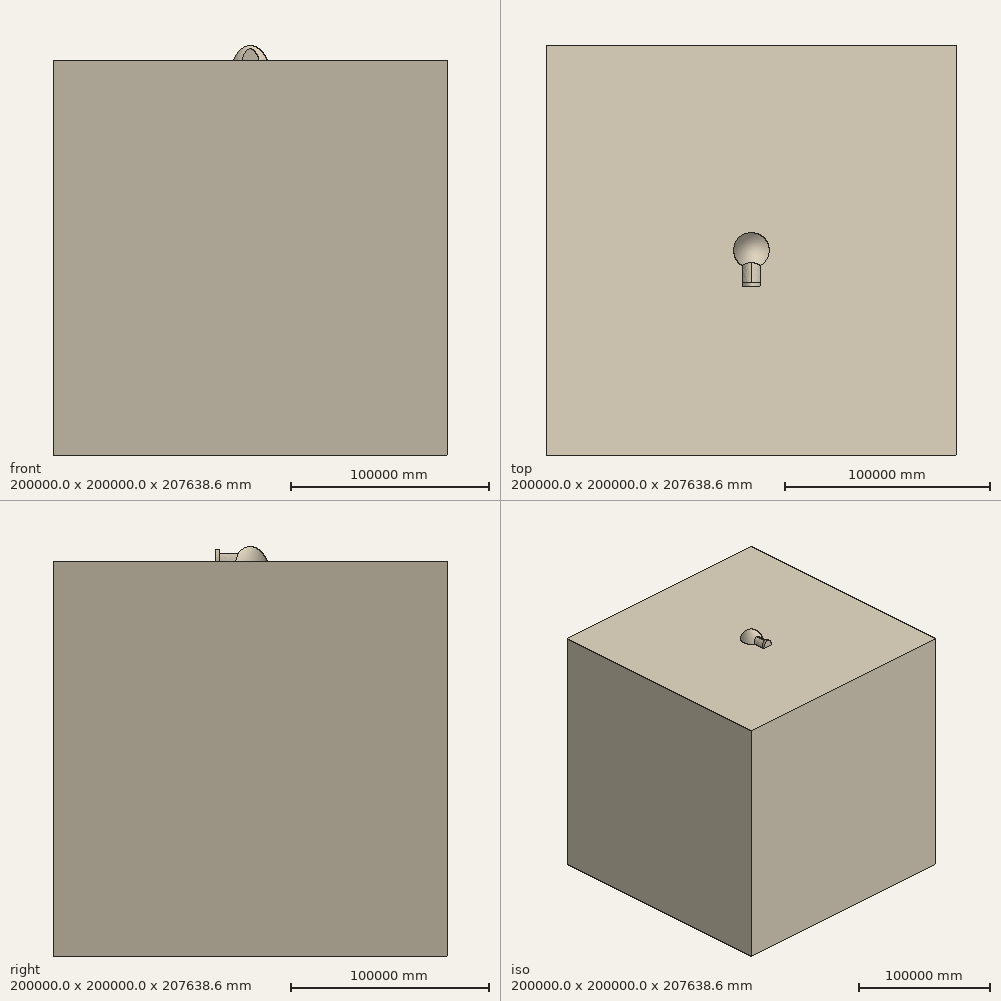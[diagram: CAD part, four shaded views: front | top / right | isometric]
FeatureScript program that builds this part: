
annotation { "Feature Type Name" : "Feature", "Feature Type Description" : "" }
export const myFeature = defineFeature(function(context is Context, id is Id, definition is map)
    precondition{}
    {
        {
            var Q0;
            Q0=qCreatedBy(makeId("Right.planeOp"),FACE);
            var sketch = newSketch(context, id + "F0", { "sketchPlane" : qUnion([Q0])});
            skFitSpline(sketch, "E0", {"points": [v(0, 7638.6) * mm, v(29.11, 7638.5) * mm, v(87.34, 7638.32) * mm, v(174.7, 7636.6) * mm, v(262.04, 7633.45) * mm, v(349.4, 7629.03) * mm, v(436.75, 7623.3) * mm, v(524.1, 7616.28) * mm, v(611.46, 7607.96) * mm, v(698.83, 7598.34) * mm, v(786.2, 7587.4) * mm, v(873.57, 7575.22) * mm, v(960.93, 7561.56) * mm, v(1048.3, 7546.64) * mm, v(1135.69, 7530.43) * mm, v(1223.06, 7512.8) * mm, v(1310.44, 7493.87) * mm, v(1397.81, 7473.6) * mm, v(1485.24, 7452.19) * mm, v(1572.58, 7429.04) * mm, v(1660, 7404.87) * mm, v(1747.4, 7379.26) * mm, v(1834.8, 7352.23) * mm, v(1922.16, 7323.74) * mm, v(2009.63, 7294.12) * mm, v(2096.98, 7262.8) * mm, v(2184.4, 7230.3) * mm, v(2271.83, 7196.4) * mm, v(2359.23, 7161.05) * mm, v(2446.66, 7124.32) * mm, v(2534.07, 7086.12) * mm, v(2621.48, 7046.47) * mm, v(2708.92, 7005.43) * mm, v(2796.34, 6962.93) * mm, v(2883.78, 6919) * mm, v(2971.2, 6873.54) * mm, v(3058.64, 6826.64) * mm, v(3146.12, 6778.32) * mm, v(3233.5, 6728.33) * mm, v(3321, 6676.98) * mm, v(3408.41, 6624) * mm, v(3495.88, 6569.56) * mm, v(3583.33, 6513.57) * mm, v(3670.8, 6456.03) * mm, v(3758.23, 6396.86) * mm, v(3845.74, 6336.2) * mm, v(3933.18, 6273.83) * mm, v(4020.62, 6209.87) * mm, v(4108.17, 6144.41) * mm, v(4195.58, 6077.13) * mm, v(4283.07, 6008.28) * mm, v(4370.6, 5937.8) * mm, v(4458.06, 5865.55) * mm, v(4545.5, 5791.58) * mm, v(4633.1, 5716.02) * mm, v(4720.52, 5638.55) * mm, v(4808.02, 5559.39) * mm, v(4895.58, 5478.53) * mm, v(4983, 5395.75) * mm, v(5070.6, 5311.3) * mm, v(5158.05, 5224.92) * mm, v(5245.61, 5136.77) * mm, v(5333.08, 5046.68) * mm, v(5420.71, 4954.83) * mm, v(5508.13, 4860.86) * mm, v(5595.7, 4765.1) * mm, v(5683.29, 4667.42) * mm, v(5770.79, 4567.66) * mm, v(5858.29, 4465.9) * mm, v(5945.9, 4362.23) * mm, v(6033.45, 4256.45) * mm, v(6120.96, 4148.6) * mm, v(6208.56, 4038.73) * mm, v(6296.18, 3926.74) * mm, v(6383.62, 3812.49) * mm, v(6471.32, 3696.22) * mm, v(6558.84, 3577.65) * mm, v(6646.38, 3456.9) * mm, v(6734.07, 3334) * mm, v(6821.65, 3208.74) * mm, v(6909.12, 3081.1) * mm, v(6996.88, 2951.3) * mm, v(7084.42, 2819.04) * mm, v(7171.98, 2684.38) * mm, v(7259.68, 2547.4) * mm, v(7347.3, 2407.92) * mm, v(7434.81, 2265.88) * mm, v(7522.6, 2121.48) * mm, v(7610.17, 1974.42) * mm, v(7697.73, 1824.78) * mm, v(7785.52, 1672.67) * mm, v(7873.1, 1517.81) * mm, v(7960.7, 1360.25) * mm, v(8048.5, 1200.06) * mm, v(8136.08, 1037.02) * mm, v(8223.73, 871.22) * mm, v(8311.5, 702.68) * mm, v(8399.14, 531.2) * mm, v(8486.77, 356.8) * mm, v(8574.63, 179.6) * mm, v(8632.51, 60.13) * mm, v(8661.64, 0) * mm]});
            skFitSpline(sketch, "E1", {"points": [v(0, 5583.5) * mm, v(20.7, 5583.4) * mm, v(62.09, 5583.2) * mm, v(124.17, 5581.72) * mm, v(186.27, 5579.52) * mm, v(248.34, 5576) * mm, v(310.44, 5571.88) * mm, v(372.53, 5566.67) * mm, v(434.62, 5560.43) * mm, v(496.71, 5553.37) * mm, v(558.8, 5545.24) * mm, v(620.87, 5536.23) * mm, v(682.98, 5526.4) * mm, v(745.05, 5515.32) * mm, v(807.13, 5503.42) * mm, v(869.25, 5490.68) * mm, v(931.3, 5476.72) * mm, v(993.4, 5461.91) * mm, v(1055.54, 5446.27) * mm, v(1117.58, 5429.42) * mm, v(1179.67, 5411.72) * mm, v(1241.74, 5393.02) * mm, v(1303.85, 5373.32) * mm, v(1365.95, 5352.61) * mm, v(1428.03, 5330.92) * mm, v(1490.11, 5308.21) * mm, v(1552.15, 5284.38) * mm, v(1614.27, 5259.7) * mm, v(1676.4, 5234) * mm, v(1738.46, 5207.2) * mm, v(1800.53, 5179.37) * mm, v(1862.6, 5150.48) * mm, v(1924.69, 5120.56) * mm, v(1986.86, 5089.7) * mm, v(2048.86, 5057.51) * mm, v(2111.05, 5024.62) * mm, v(2173.01, 4990.3) * mm, v(2235.17, 4955.18) * mm, v(2297.21, 4918.72) * mm, v(2359.34, 4881.33) * mm, v(2421.46, 4842.87) * mm, v(2483.46, 4803.09) * mm, v(2545.55, 4762.32) * mm, v(2607.69, 4720.42) * mm, v(2669.75, 4677.29) * mm, v(2731.88, 4633.13) * mm, v(2793.9, 4587.66) * mm, v(2855.96, 4541.07) * mm, v(2918.13, 4493.39) * mm, v(2980.15, 4444.35) * mm, v(3042.32, 4394.3) * mm, v(3104.3, 4342.8) * mm, v(3166.43, 4290.26) * mm, v(3228.49, 4236.33) * mm, v(3290.62, 4181.23) * mm, v(3352.72, 4124.85) * mm, v(3414.72, 4067.08) * mm, v(3476.83, 4008.11) * mm, v(3538.92, 3947.8) * mm, v(3601.06, 3886.2) * mm, v(3663.11, 3823.17) * mm, v(3725.26, 3758.91) * mm, v(3787.2, 3693.12) * mm, v(3849.39, 3626.16) * mm, v(3911.44, 3557.64) * mm, v(3973.54, 3487.73) * mm, v(4035.68, 3416.46) * mm, v(4097.63, 3343.58) * mm, v(4159.78, 3269.41) * mm, v(4221.87, 3193.7) * mm, v(4283.96, 3116.48) * mm, v(4346.1, 3037.8) * mm, v(4408.04, 2957.44) * mm, v(4470.2, 2875.66) * mm, v(4532.28, 2792.25) * mm, v(4594.37, 2707.23) * mm, v(4656.52, 2620.65) * mm, v(4718.46, 2532.3) * mm, v(4780.57, 2442.42) * mm, v(4842.72, 2350.88) * mm, v(4904.79, 2257.6) * mm, v(4966.88, 2162.58) * mm, v(5029.02, 2065.9) * mm, v(5091, 1967.32) * mm, v(5153.08, 1867.07) * mm, v(5215.23, 1765.02) * mm, v(5277.3, 1661.1) * mm, v(5339.44, 1555.34) * mm, v(5401.36, 1447.59) * mm, v(5463.54, 1338.08) * mm, v(5525.6, 1226.58) * mm, v(5587.74, 1113.15) * mm, v(5649.82, 997.72) * mm, v(5711.8, 880.2) * mm, v(5773.93, 760.75) * mm, v(5836.02, 639.2) * mm, v(5898.12, 515.55) * mm, v(5960.25, 389.81) * mm, v(6022.2, 261.83) * mm, v(6084.37, 131.79) * mm, v(6125.36, 44.13) * mm, v(6146, 0) * mm]});
            skLineSegment(sketch, "E2", {"start": v(6146, 0) * mm, "end": v(8661.64, 0) * mm});
            skLineSegment(sketch, "E3", {"start": v(0, 5583.5) * mm, "end": v(0, 7638.6) * mm});
            skLineSegment(sketch, "E4", {"start": v(0, 0) * mm, "end": v(13207.23, 0) * mm});
            skLineSegment(sketch, "E5", {"start": v(0, 0) * mm, "end": v(0, 9039.67) * mm, "construction": true});
            skSolve(sketch);
        }
        {
            var Q0;
            Q0=qSketchRegion(id+"F0",true);
            var Q1;
            Q1=sQuery(id+"F0.wireOp",EDGE,"E3");
            revolve(context, id + "F1", {"surfaceOperationType" : NewSurfaceOperationType.NEW, "entities" : qUnion([Q0]), "axis" : qUnion([Q1]), "revolveType" : RevolveType.FULL});
        }
        {
            var Q0;
            Q0=qCreatedBy(makeId("Front.planeOp"),FACE);
            var sketch = newSketch(context, id + "F2", { "sketchPlane" : qUnion([Q0])});
            skFitSpline(sketch, "E6", {"points": [v(-2323.2, 0) * mm, v(-2315.44, 23.67) * mm, v(-2300.04, 70.61) * mm, v(-2276.5, 140.2) * mm, v(-2252.98, 208.44) * mm, v(-2229.63, 275.42) * mm, v(-2206.1, 341.03) * mm, v(-2182.58, 405.35) * mm, v(-2159.23, 468.49) * mm, v(-2135.7, 530.32) * mm, v(-2112.18, 590.94) * mm, v(-2088.82, 650.42) * mm, v(-2065.3, 708.67) * mm, v(-2041.78, 765.76) * mm, v(-2018.42, 821.79) * mm, v(-1994.9, 876.63) * mm, v(-1971.37, 930.37) * mm, v(-1948.01, 983.11) * mm, v(-1924.53, 1034.72) * mm, v(-1900.94, 1085.25) * mm, v(-1877.65, 1134.87) * mm, v(-1854.07, 1183.38) * mm, v(-1830.58, 1230.94) * mm, v(-1807.22, 1277.6) * mm, v(-1783.68, 1323.2) * mm, v(-1760.2, 1367.85) * mm, v(-1736.8, 1411.63) * mm, v(-1713.26, 1454.42) * mm, v(-1689.8, 1496.37) * mm, v(-1666.38, 1537.46) * mm, v(-1642.9, 1577.62) * mm, v(-1619.36, 1616.9) * mm, v(-1595.99, 1655.47) * mm, v(-1572.51, 1693.13) * mm, v(-1548.93, 1729.93) * mm, v(-1525.63, 1766.08) * mm, v(-1502.05, 1801.27) * mm, v(-1478.58, 1835.73) * mm, v(-1455.2, 1869.5) * mm, v(-1431.66, 1902.38) * mm, v(-1408.17, 1934.6) * mm, v(-1384.7, 1966.05) * mm, v(-1361.24, 1996.83) * mm, v(-1337.8, 2026.9) * mm, v(-1314.26, 2056.17) * mm, v(-1290.85, 2084.85) * mm, v(-1267.38, 2112.82) * mm, v(-1243.87, 2140.09) * mm, v(-1220.45, 2166.76) * mm, v(-1196.98, 2192.73) * mm, v(-1173.44, 2218) * mm, v(-1150.09, 2242.78) * mm, v(-1126.51, 2266.74) * mm, v(-1103.09, 2290.22) * mm, v(-1079.65, 2313.09) * mm, v(-1056.12, 2335.26) * mm, v(-1032.7, 2356.94) * mm, v(-1009.21, 2378) * mm, v(-985.76, 2398.47) * mm, v(-962.3, 2418.38) * mm, v(-938.8, 2437.68) * mm, v(-915.36, 2456.49) * mm, v(-891.9, 2474.7) * mm, v(-868.36, 2492.27) * mm, v(-845, 2509.53) * mm, v(-821.42, 2525.97) * mm, v(-798.03, 2542.13) * mm, v(-774.52, 2557.6) * mm, v(-751.06, 2572.61) * mm, v(-727.59, 2587.12) * mm, v(-704.12, 2601.12) * mm, v(-680.65, 2614.62) * mm, v(-657.18, 2627.62) * mm, v(-633.71, 2640.13) * mm, v(-610.24, 2652.13) * mm, v(-586.77, 2663.64) * mm, v(-563.28, 2674.62) * mm, v(-539.86, 2685.27) * mm, v(-516.34, 2695.22) * mm, v(-492.88, 2704.84) * mm, v(-469.42, 2714.06) * mm, v(-445.95, 2722.75) * mm, v(-422.48, 2730.96) * mm, v(-399, 2738.64) * mm, v(-375.54, 2745.97) * mm, v(-352.05, 2752.75) * mm, v(-328.58, 2759.14) * mm, v(-305.15, 2765.21) * mm, v(-281.63, 2770.51) * mm, v(-258.19, 2775.69) * mm, v(-234.72, 2780.29) * mm, v(-211.22, 2784.31) * mm, v(-187.79, 2788.24) * mm, v(-164.28, 2791.31) * mm, v(-140.83, 2794.3) * mm, v(-117.35, 2796.68) * mm, v(-93.88, 2798.56) * mm, v(-70.41, 2800.07) * mm, v(-46.94, 2801.16) * mm, v(-23.47, 2801.9) * mm, v(0, 2802.05) * mm, v(23.47, 2801.9) * mm, v(46.94, 2801.16) * mm, v(70.41, 2800.07) * mm, v(93.88, 2798.56) * mm, v(117.35, 2796.68) * mm, v(140.83, 2794.3) * mm, v(164.28, 2791.31) * mm, v(187.79, 2788.24) * mm, v(211.22, 2784.31) * mm, v(234.72, 2780.29) * mm, v(258.19, 2775.69) * mm, v(281.63, 2770.51) * mm, v(305.15, 2765.21) * mm, v(328.58, 2759.14) * mm, v(352.05, 2752.75) * mm, v(375.54, 2745.97) * mm, v(399, 2738.64) * mm, v(422.48, 2730.96) * mm, v(445.95, 2722.75) * mm, v(469.43, 2714.06) * mm, v(492.88, 2704.84) * mm, v(516.34, 2695.22) * mm, v(539.86, 2685.27) * mm, v(563.28, 2674.62) * mm, v(586.77, 2663.64) * mm, v(610.24, 2652.13) * mm, v(633.71, 2640.13) * mm, v(657.18, 2627.62) * mm, v(680.65, 2614.62) * mm, v(704.12, 2601.12) * mm, v(727.59, 2587.12) * mm, v(751.06, 2572.61) * mm, v(774.52, 2557.6) * mm, v(798.03, 2542.13) * mm, v(821.42, 2525.97) * mm, v(845, 2509.53) * mm, v(868.36, 2492.27) * mm, v(891.9, 2474.7) * mm, v(915.36, 2456.49) * mm, v(938.8, 2437.68) * mm, v(962.3, 2418.38) * mm, v(985.76, 2398.47) * mm, v(1009.21, 2378) * mm, v(1032.7, 2356.94) * mm, v(1056.12, 2335.26) * mm, v(1079.65, 2313.09) * mm, v(1103.09, 2290.22) * mm, v(1126.51, 2266.74) * mm, v(1150.09, 2242.78) * mm, v(1173.44, 2218) * mm, v(1196.98, 2192.73) * mm, v(1220.45, 2166.76) * mm, v(1243.87, 2140.09) * mm, v(1267.38, 2112.82) * mm, v(1290.85, 2084.85) * mm, v(1314.26, 2056.17) * mm, v(1337.8, 2026.9) * mm, v(1361.24, 1996.83) * mm, v(1384.7, 1966.05) * mm, v(1408.17, 1934.6) * mm, v(1431.66, 1902.38) * mm, v(1455.2, 1869.5) * mm, v(1478.58, 1835.73) * mm, v(1502.05, 1801.27) * mm, v(1525.63, 1766.08) * mm, v(1548.93, 1729.93) * mm, v(1572.51, 1693.13) * mm, v(1595.99, 1655.47) * mm, v(1619.36, 1616.9) * mm, v(1642.9, 1577.62) * mm, v(1666.38, 1537.46) * mm, v(1689.8, 1496.37) * mm, v(1713.26, 1454.42) * mm, v(1736.8, 1411.63) * mm, v(1760.2, 1367.85) * mm, v(1783.68, 1323.2) * mm, v(1807.22, 1277.6) * mm, v(1830.58, 1230.94) * mm, v(1854.07, 1183.38) * mm, v(1877.65, 1134.87) * mm, v(1900.94, 1085.25) * mm, v(1924.53, 1034.72) * mm, v(1948.01, 983.11) * mm, v(1971.37, 930.37) * mm, v(1994.9, 876.63) * mm, v(2018.42, 821.79) * mm, v(2041.78, 765.76) * mm, v(2065.3, 708.67) * mm, v(2088.82, 650.42) * mm, v(2112.18, 590.94) * mm, v(2135.7, 530.32) * mm, v(2159.23, 468.49) * mm, v(2182.58, 405.35) * mm, v(2206.1, 341.03) * mm, v(2229.63, 275.42) * mm, v(2252.98, 208.44) * mm, v(2276.5, 140.2) * mm, v(2300.04, 70.61) * mm, v(2315.44, 23.67) * mm, v(2323.2, 0) * mm]});
            skLineSegment(sketch, "E7", {"start": v(0, 0) * mm, "end": v(0, 3094.92) * mm, "construction": true});
            skLineSegment(sketch, "E8", {"start": v(-2323.2, 0) * mm, "end": v(2323.2, 0) * mm});
            skSolve(sketch);
        }
        {
            var Q0;
            Q0=qSketchRegion(id+"F2",true);
            extrude(context, id + "F3", {"entities" : qUnion([Q0]), "operationType" : NewBodyOperationType.REMOVE, "depth" : 10020 * mm, "offsetDistance" : 25 * mm});
        }
        {
            var Q0;
            Q0=qCreatedBy(makeId("Front.planeOp"),FACE);
            var sketch = newSketch(context, id + "F4", { "sketchPlane" : qUnion([Q0])});
            skFitSpline(sketch, "E9.0", {"points": [v(-2323.2, 0) * mm, v(-2315.44, 23.67) * mm, v(-2300.04, 70.61) * mm, v(-2276.5, 140.2) * mm, v(-2252.98, 208.44) * mm, v(-2229.63, 275.42) * mm, v(-2206.1, 341.03) * mm, v(-2182.58, 405.35) * mm, v(-2159.23, 468.49) * mm, v(-2135.7, 530.32) * mm, v(-2112.18, 590.94) * mm, v(-2088.82, 650.42) * mm, v(-2065.3, 708.67) * mm, v(-2041.78, 765.76) * mm, v(-2018.42, 821.79) * mm, v(-1994.9, 876.63) * mm, v(-1971.37, 930.37) * mm, v(-1948.01, 983.11) * mm, v(-1924.53, 1034.72) * mm, v(-1900.94, 1085.25) * mm, v(-1877.65, 1134.87) * mm, v(-1854.07, 1183.38) * mm, v(-1830.58, 1230.94) * mm, v(-1807.22, 1277.6) * mm, v(-1783.68, 1323.2) * mm, v(-1760.2, 1367.85) * mm, v(-1736.8, 1411.63) * mm, v(-1713.26, 1454.42) * mm, v(-1689.8, 1496.37) * mm, v(-1666.38, 1537.46) * mm, v(-1642.9, 1577.62) * mm, v(-1619.36, 1616.9) * mm, v(-1595.99, 1655.47) * mm, v(-1572.51, 1693.13) * mm, v(-1548.93, 1729.93) * mm, v(-1525.63, 1766.08) * mm, v(-1502.05, 1801.27) * mm, v(-1478.58, 1835.73) * mm, v(-1455.2, 1869.5) * mm, v(-1431.66, 1902.38) * mm, v(-1408.17, 1934.6) * mm, v(-1384.7, 1966.05) * mm, v(-1361.24, 1996.83) * mm, v(-1337.8, 2026.9) * mm, v(-1314.26, 2056.17) * mm, v(-1290.85, 2084.85) * mm, v(-1267.38, 2112.82) * mm, v(-1243.87, 2140.09) * mm, v(-1220.45, 2166.76) * mm, v(-1196.98, 2192.73) * mm, v(-1173.44, 2218) * mm, v(-1150.09, 2242.78) * mm, v(-1126.51, 2266.74) * mm, v(-1103.09, 2290.22) * mm, v(-1079.65, 2313.09) * mm, v(-1056.12, 2335.26) * mm, v(-1032.7, 2356.94) * mm, v(-1009.21, 2378) * mm, v(-985.76, 2398.47) * mm, v(-962.3, 2418.38) * mm, v(-938.8, 2437.68) * mm, v(-915.36, 2456.49) * mm, v(-891.9, 2474.7) * mm, v(-868.36, 2492.27) * mm, v(-845, 2509.53) * mm, v(-821.42, 2525.97) * mm, v(-798.03, 2542.13) * mm, v(-774.52, 2557.6) * mm, v(-751.06, 2572.61) * mm, v(-727.59, 2587.12) * mm, v(-704.12, 2601.12) * mm, v(-680.65, 2614.62) * mm, v(-657.18, 2627.62) * mm, v(-633.71, 2640.13) * mm, v(-610.24, 2652.13) * mm, v(-586.77, 2663.64) * mm, v(-563.28, 2674.62) * mm, v(-539.86, 2685.27) * mm, v(-516.34, 2695.22) * mm, v(-492.88, 2704.84) * mm, v(-469.42, 2714.06) * mm, v(-445.95, 2722.75) * mm, v(-422.48, 2730.96) * mm, v(-399, 2738.64) * mm, v(-375.54, 2745.97) * mm, v(-352.05, 2752.75) * mm, v(-328.58, 2759.14) * mm, v(-305.15, 2765.21) * mm, v(-281.63, 2770.51) * mm, v(-258.19, 2775.69) * mm, v(-234.72, 2780.29) * mm, v(-211.22, 2784.31) * mm, v(-187.79, 2788.24) * mm, v(-164.28, 2791.31) * mm, v(-140.83, 2794.3) * mm, v(-117.35, 2796.68) * mm, v(-93.88, 2798.56) * mm, v(-70.41, 2800.07) * mm, v(-46.94, 2801.16) * mm, v(-23.47, 2801.9) * mm, v(0, 2802.05) * mm, v(23.47, 2801.9) * mm, v(46.94, 2801.16) * mm, v(70.41, 2800.07) * mm, v(93.88, 2798.56) * mm, v(117.35, 2796.68) * mm, v(140.83, 2794.3) * mm, v(164.28, 2791.31) * mm, v(187.79, 2788.24) * mm, v(211.22, 2784.31) * mm, v(234.72, 2780.29) * mm, v(258.19, 2775.69) * mm, v(281.63, 2770.51) * mm, v(305.15, 2765.21) * mm, v(328.58, 2759.14) * mm, v(352.05, 2752.75) * mm, v(375.54, 2745.97) * mm, v(399, 2738.64) * mm, v(422.48, 2730.96) * mm, v(445.95, 2722.75) * mm, v(469.43, 2714.06) * mm, v(492.88, 2704.84) * mm, v(516.34, 2695.22) * mm, v(539.86, 2685.27) * mm, v(563.28, 2674.62) * mm, v(586.77, 2663.64) * mm, v(610.24, 2652.13) * mm, v(633.71, 2640.13) * mm, v(657.18, 2627.62) * mm, v(680.65, 2614.62) * mm, v(704.12, 2601.12) * mm, v(727.59, 2587.12) * mm, v(751.06, 2572.61) * mm, v(774.52, 2557.6) * mm, v(798.03, 2542.13) * mm, v(821.42, 2525.97) * mm, v(845, 2509.53) * mm, v(868.36, 2492.27) * mm, v(891.9, 2474.7) * mm, v(915.36, 2456.49) * mm, v(938.8, 2437.68) * mm, v(962.3, 2418.38) * mm, v(985.76, 2398.47) * mm, v(1009.21, 2378) * mm, v(1032.7, 2356.94) * mm, v(1056.12, 2335.26) * mm, v(1079.65, 2313.09) * mm, v(1103.09, 2290.22) * mm, v(1126.51, 2266.74) * mm, v(1150.09, 2242.78) * mm, v(1173.44, 2218) * mm, v(1196.98, 2192.73) * mm, v(1220.45, 2166.76) * mm, v(1243.87, 2140.09) * mm, v(1267.38, 2112.82) * mm, v(1290.85, 2084.85) * mm, v(1314.26, 2056.17) * mm, v(1337.8, 2026.9) * mm, v(1361.24, 1996.83) * mm, v(1384.7, 1966.05) * mm, v(1408.17, 1934.6) * mm, v(1431.66, 1902.38) * mm, v(1455.2, 1869.5) * mm, v(1478.58, 1835.73) * mm, v(1502.05, 1801.27) * mm, v(1525.63, 1766.08) * mm, v(1548.93, 1729.93) * mm, v(1572.51, 1693.13) * mm, v(1595.99, 1655.47) * mm, v(1619.36, 1616.9) * mm, v(1642.9, 1577.62) * mm, v(1666.38, 1537.46) * mm, v(1689.8, 1496.37) * mm, v(1713.26, 1454.42) * mm, v(1736.8, 1411.63) * mm, v(1760.2, 1367.85) * mm, v(1783.68, 1323.2) * mm, v(1807.22, 1277.6) * mm, v(1830.58, 1230.94) * mm, v(1854.07, 1183.38) * mm, v(1877.65, 1134.87) * mm, v(1900.94, 1085.25) * mm, v(1924.53, 1034.72) * mm, v(1948.01, 983.11) * mm, v(1971.37, 930.37) * mm, v(1994.9, 876.63) * mm, v(2018.42, 821.79) * mm, v(2041.78, 765.76) * mm, v(2065.3, 708.67) * mm, v(2088.82, 650.42) * mm, v(2112.18, 590.94) * mm, v(2135.7, 530.32) * mm, v(2159.23, 468.49) * mm, v(2182.58, 405.35) * mm, v(2206.1, 341.03) * mm, v(2229.63, 275.42) * mm, v(2252.98, 208.44) * mm, v(2276.5, 140.2) * mm, v(2300.04, 70.61) * mm, v(2315.44, 23.67) * mm, v(2323.2, 0) * mm]});
            skLineSegment(sketch, "E10", {"start": v(-2323.2, 0) * mm, "end": v(-4323.2, 0) * mm});
            skLineSegment(sketch, "E11", {"start": v(2323.2, 0) * mm, "end": v(4323.2, 0) * mm});
            skLineSegment(sketch, "E12", {"start": v(0, 2802) * mm, "end": v(0, 4302) * mm});
            skFitSpline(sketch, "E13", {"points": [v(-4323.2, 0) * mm, v(0, 4302) * mm, v(4323.2, 0) * mm], "startDerivative": vector(5539.2, 16200) * mm, "endDerivative": vector(5539.2, -16200) * mm});
            skFitSpline(sketch, "E14.0", {"points": [v(-2323.2, 0) * mm, v(-2315.44, 23.67) * mm, v(-2300.04, 70.61) * mm, v(-2276.5, 140.2) * mm, v(-2252.98, 208.44) * mm, v(-2229.63, 275.42) * mm, v(-2206.1, 341.03) * mm, v(-2182.58, 405.35) * mm, v(-2159.23, 468.49) * mm, v(-2135.7, 530.32) * mm, v(-2112.18, 590.94) * mm, v(-2088.82, 650.42) * mm, v(-2065.3, 708.67) * mm, v(-2041.78, 765.76) * mm, v(-2018.42, 821.79) * mm, v(-1994.9, 876.63) * mm, v(-1971.37, 930.37) * mm, v(-1948.01, 983.11) * mm, v(-1924.53, 1034.72) * mm, v(-1900.94, 1085.25) * mm, v(-1877.65, 1134.87) * mm, v(-1854.07, 1183.38) * mm, v(-1830.58, 1230.94) * mm, v(-1807.22, 1277.6) * mm, v(-1783.68, 1323.2) * mm, v(-1760.2, 1367.85) * mm, v(-1736.8, 1411.63) * mm, v(-1713.26, 1454.42) * mm, v(-1689.8, 1496.37) * mm, v(-1666.38, 1537.46) * mm, v(-1642.9, 1577.62) * mm, v(-1619.36, 1616.9) * mm, v(-1595.99, 1655.47) * mm, v(-1572.51, 1693.13) * mm, v(-1548.93, 1729.93) * mm, v(-1525.63, 1766.08) * mm, v(-1502.05, 1801.27) * mm, v(-1478.58, 1835.73) * mm, v(-1455.2, 1869.5) * mm, v(-1431.66, 1902.38) * mm, v(-1408.17, 1934.6) * mm, v(-1384.7, 1966.05) * mm, v(-1361.24, 1996.83) * mm, v(-1337.8, 2026.9) * mm, v(-1314.26, 2056.17) * mm, v(-1290.85, 2084.85) * mm, v(-1267.38, 2112.82) * mm, v(-1243.87, 2140.09) * mm, v(-1220.45, 2166.76) * mm, v(-1196.98, 2192.73) * mm, v(-1173.44, 2218) * mm, v(-1150.09, 2242.78) * mm, v(-1126.51, 2266.74) * mm, v(-1103.09, 2290.22) * mm, v(-1079.65, 2313.09) * mm, v(-1056.12, 2335.26) * mm, v(-1032.7, 2356.94) * mm, v(-1009.21, 2378) * mm, v(-985.76, 2398.47) * mm, v(-962.3, 2418.38) * mm, v(-938.8, 2437.68) * mm, v(-915.36, 2456.49) * mm, v(-891.9, 2474.7) * mm, v(-868.36, 2492.27) * mm, v(-845, 2509.53) * mm, v(-821.42, 2525.97) * mm, v(-798.03, 2542.13) * mm, v(-774.52, 2557.6) * mm, v(-751.06, 2572.61) * mm, v(-727.59, 2587.12) * mm, v(-704.12, 2601.12) * mm, v(-680.65, 2614.62) * mm, v(-657.18, 2627.62) * mm, v(-633.71, 2640.13) * mm, v(-610.24, 2652.13) * mm, v(-586.77, 2663.64) * mm, v(-563.28, 2674.62) * mm, v(-539.86, 2685.27) * mm, v(-516.34, 2695.22) * mm, v(-492.88, 2704.84) * mm, v(-469.42, 2714.06) * mm, v(-445.95, 2722.75) * mm, v(-422.48, 2730.96) * mm, v(-399, 2738.64) * mm, v(-375.54, 2745.97) * mm, v(-352.05, 2752.75) * mm, v(-328.58, 2759.14) * mm, v(-305.15, 2765.21) * mm, v(-281.63, 2770.51) * mm, v(-258.19, 2775.69) * mm, v(-234.72, 2780.29) * mm, v(-211.22, 2784.31) * mm, v(-187.79, 2788.24) * mm, v(-164.28, 2791.31) * mm, v(-140.83, 2794.3) * mm, v(-117.35, 2796.68) * mm, v(-93.88, 2798.56) * mm, v(-70.41, 2800.07) * mm, v(-46.94, 2801.16) * mm, v(-23.47, 2801.9) * mm, v(0, 2802.05) * mm, v(23.47, 2801.9) * mm, v(46.94, 2801.16) * mm, v(70.41, 2800.07) * mm, v(93.88, 2798.56) * mm, v(117.35, 2796.68) * mm, v(140.83, 2794.3) * mm, v(164.28, 2791.31) * mm, v(187.79, 2788.24) * mm, v(211.22, 2784.31) * mm, v(234.72, 2780.29) * mm, v(258.19, 2775.69) * mm, v(281.63, 2770.51) * mm, v(305.15, 2765.21) * mm, v(328.58, 2759.14) * mm, v(352.05, 2752.75) * mm, v(375.54, 2745.97) * mm, v(399, 2738.64) * mm, v(422.48, 2730.96) * mm, v(445.95, 2722.75) * mm, v(469.43, 2714.06) * mm, v(492.88, 2704.84) * mm, v(516.34, 2695.22) * mm, v(539.86, 2685.27) * mm, v(563.28, 2674.62) * mm, v(586.77, 2663.64) * mm, v(610.24, 2652.13) * mm, v(633.71, 2640.13) * mm, v(657.18, 2627.62) * mm, v(680.65, 2614.62) * mm, v(704.12, 2601.12) * mm, v(727.59, 2587.12) * mm, v(751.06, 2572.61) * mm, v(774.52, 2557.6) * mm, v(798.03, 2542.13) * mm, v(821.42, 2525.97) * mm, v(845, 2509.53) * mm, v(868.36, 2492.27) * mm, v(891.9, 2474.7) * mm, v(915.36, 2456.49) * mm, v(938.8, 2437.68) * mm, v(962.3, 2418.38) * mm, v(985.76, 2398.47) * mm, v(1009.21, 2378) * mm, v(1032.7, 2356.94) * mm, v(1056.12, 2335.26) * mm, v(1079.65, 2313.09) * mm, v(1103.09, 2290.22) * mm, v(1126.51, 2266.74) * mm, v(1150.09, 2242.78) * mm, v(1173.44, 2218) * mm, v(1196.98, 2192.73) * mm, v(1220.45, 2166.76) * mm, v(1243.87, 2140.09) * mm, v(1267.38, 2112.82) * mm, v(1290.85, 2084.85) * mm, v(1314.26, 2056.17) * mm, v(1337.8, 2026.9) * mm, v(1361.24, 1996.83) * mm, v(1384.7, 1966.05) * mm, v(1408.17, 1934.6) * mm, v(1431.66, 1902.38) * mm, v(1455.2, 1869.5) * mm, v(1478.58, 1835.73) * mm, v(1502.05, 1801.27) * mm, v(1525.63, 1766.08) * mm, v(1548.93, 1729.93) * mm, v(1572.51, 1693.13) * mm, v(1595.99, 1655.47) * mm, v(1619.36, 1616.9) * mm, v(1642.9, 1577.62) * mm, v(1666.38, 1537.46) * mm, v(1689.8, 1496.37) * mm, v(1713.26, 1454.42) * mm, v(1736.8, 1411.63) * mm, v(1760.2, 1367.85) * mm, v(1783.68, 1323.2) * mm, v(1807.22, 1277.6) * mm, v(1830.58, 1230.94) * mm, v(1854.07, 1183.38) * mm, v(1877.65, 1134.87) * mm, v(1900.94, 1085.25) * mm, v(1924.53, 1034.72) * mm, v(1948.01, 983.11) * mm, v(1971.37, 930.37) * mm, v(1994.9, 876.63) * mm, v(2018.42, 821.79) * mm, v(2041.78, 765.76) * mm, v(2065.3, 708.67) * mm, v(2088.82, 650.42) * mm, v(2112.18, 590.94) * mm, v(2135.7, 530.32) * mm, v(2159.23, 468.49) * mm, v(2182.58, 405.35) * mm, v(2206.1, 341.03) * mm, v(2229.63, 275.42) * mm, v(2252.98, 208.44) * mm, v(2276.5, 140.2) * mm, v(2300.04, 70.61) * mm, v(2315.44, 23.67) * mm, v(2323.2, 0) * mm]});
            skSolve(sketch);
        }
        {
            var Q0;
            {var subQ0=sQuery(id+"F4.wireOp",EDGE,"E10");Q0=makeQuery(id+"F4.imprint","IMPRINT",FACE,{"disambiguationData":[TD([[makeQuery(id+"F4.imprint","IMPRINT",EDGE,{"derivedFrom":subQ0}),-1.0]])]});}
            var Q1;
            {var subQ0=sQuery(id+"F4.wireOp",EDGE,"E11");Q1=makeQuery(id+"F4.imprint","IMPRINT",FACE,{"disambiguationData":[TD([[makeQuery(id+"F4.imprint","IMPRINT",EDGE,{"derivedFrom":subQ0}),1.0]])]});}
            var Q2;
            Q2=sQuery(id+"F4.wireOp",EDGE,"E13");
            var Q3;
            Q3=sQuery(id+"F4.wireOp",EDGE,"E14.0");
            var Q4;
            Q4=sQuery(id+"F4.wireOp",EDGE,"E10");
            var Q5;
            Q5=sQuery(id+"F4.wireOp",EDGE,"E11");
            extrude(context, id + "F5", {"entities" : qUnion([Q0, Q1]), "operationType" : NewBodyOperationType.ADD, "surfaceOperationType" : NewSurfaceOperationType.ADD, "surfaceEntities" : qUnion([Q2, Q3, Q4, Q5]), "depth" : 17622 * mm, "offsetDistance" : 25 * mm});
        }
        {
            var Q0;
            Q0=makeQuery(id+"F5.opExtrude","CAP_FACE",FACE,{"disambiguationData":[OSD([sQuery(id+"F4.wireOp",EDGE,"E10"),sQuery(id+"F4.wireOp",EDGE,"E11"),sQuery(id+"F4.wireOp",EDGE,"E13"),sQuery(id+"F4.wireOp",EDGE,"E14.0")])],"isStart":true});
            var sketch = newSketch(context, id + "F6", { "sketchPlane" : qUnion([Q0])});
            skFitSpline(sketch, "E15.0.0", {"points": [v(-2323.2, 0) * mm, v(-2315.44, 23.67) * mm, v(-2300.04, 70.61) * mm, v(-2276.5, 140.2) * mm, v(-2252.98, 208.44) * mm, v(-2229.63, 275.42) * mm, v(-2206.1, 341.03) * mm, v(-2182.58, 405.35) * mm, v(-2159.23, 468.49) * mm, v(-2135.7, 530.32) * mm, v(-2112.18, 590.94) * mm, v(-2088.82, 650.42) * mm, v(-2065.3, 708.67) * mm, v(-2041.78, 765.76) * mm, v(-2018.42, 821.79) * mm, v(-1994.9, 876.63) * mm, v(-1971.37, 930.37) * mm, v(-1948.01, 983.11) * mm, v(-1924.53, 1034.72) * mm, v(-1900.94, 1085.25) * mm, v(-1877.65, 1134.87) * mm, v(-1854.07, 1183.38) * mm, v(-1830.58, 1230.94) * mm, v(-1807.22, 1277.6) * mm, v(-1783.68, 1323.2) * mm, v(-1760.2, 1367.85) * mm, v(-1736.8, 1411.63) * mm, v(-1713.26, 1454.42) * mm, v(-1689.8, 1496.37) * mm, v(-1666.38, 1537.46) * mm, v(-1642.9, 1577.62) * mm, v(-1619.36, 1616.9) * mm, v(-1595.99, 1655.47) * mm, v(-1572.51, 1693.13) * mm, v(-1548.93, 1729.93) * mm, v(-1525.63, 1766.08) * mm, v(-1502.05, 1801.27) * mm, v(-1478.58, 1835.73) * mm, v(-1455.2, 1869.5) * mm, v(-1431.66, 1902.38) * mm, v(-1408.17, 1934.6) * mm, v(-1384.7, 1966.05) * mm, v(-1361.24, 1996.83) * mm, v(-1337.8, 2026.9) * mm, v(-1314.26, 2056.17) * mm, v(-1290.85, 2084.85) * mm, v(-1267.38, 2112.82) * mm, v(-1243.87, 2140.09) * mm, v(-1220.45, 2166.76) * mm, v(-1196.98, 2192.73) * mm, v(-1173.44, 2218) * mm, v(-1150.09, 2242.78) * mm, v(-1126.51, 2266.74) * mm, v(-1103.09, 2290.22) * mm, v(-1079.65, 2313.09) * mm, v(-1056.12, 2335.26) * mm, v(-1032.7, 2356.94) * mm, v(-1009.21, 2378) * mm, v(-985.76, 2398.47) * mm, v(-962.3, 2418.38) * mm, v(-938.8, 2437.68) * mm, v(-915.36, 2456.49) * mm, v(-891.9, 2474.7) * mm, v(-868.36, 2492.27) * mm, v(-845, 2509.53) * mm, v(-821.42, 2525.97) * mm, v(-798.03, 2542.13) * mm, v(-774.52, 2557.6) * mm, v(-751.06, 2572.61) * mm, v(-727.59, 2587.12) * mm, v(-704.12, 2601.12) * mm, v(-680.65, 2614.62) * mm, v(-657.18, 2627.62) * mm, v(-633.71, 2640.13) * mm, v(-610.24, 2652.13) * mm, v(-586.77, 2663.64) * mm, v(-563.28, 2674.62) * mm, v(-539.86, 2685.27) * mm, v(-516.34, 2695.22) * mm, v(-492.88, 2704.84) * mm, v(-469.43, 2714.06) * mm, v(-445.95, 2722.75) * mm, v(-422.48, 2730.96) * mm, v(-399, 2738.64) * mm, v(-375.54, 2745.97) * mm, v(-352.05, 2752.75) * mm, v(-328.58, 2759.14) * mm, v(-305.15, 2765.21) * mm, v(-281.63, 2770.51) * mm, v(-258.19, 2775.69) * mm, v(-234.72, 2780.29) * mm, v(-211.22, 2784.31) * mm, v(-187.79, 2788.24) * mm, v(-164.28, 2791.31) * mm, v(-140.83, 2794.3) * mm, v(-117.35, 2796.68) * mm, v(-93.88, 2798.56) * mm, v(-70.41, 2800.07) * mm, v(-46.94, 2801.16) * mm, v(-23.47, 2801.9) * mm, v(0, 2802.05) * mm, v(23.47, 2801.9) * mm, v(46.94, 2801.16) * mm, v(70.41, 2800.07) * mm, v(93.88, 2798.56) * mm, v(117.35, 2796.68) * mm, v(140.83, 2794.3) * mm, v(164.28, 2791.31) * mm, v(187.79, 2788.24) * mm, v(211.22, 2784.31) * mm, v(234.72, 2780.29) * mm, v(258.19, 2775.69) * mm, v(281.63, 2770.51) * mm, v(305.15, 2765.21) * mm, v(328.58, 2759.14) * mm, v(352.05, 2752.75) * mm, v(375.54, 2745.97) * mm, v(399, 2738.64) * mm, v(422.48, 2730.96) * mm, v(445.95, 2722.75) * mm, v(469.42, 2714.06) * mm, v(492.88, 2704.84) * mm, v(516.34, 2695.22) * mm, v(539.86, 2685.27) * mm, v(563.28, 2674.62) * mm, v(586.77, 2663.64) * mm, v(610.24, 2652.13) * mm, v(633.71, 2640.13) * mm, v(657.18, 2627.62) * mm, v(680.65, 2614.62) * mm, v(704.12, 2601.12) * mm, v(727.59, 2587.12) * mm, v(751.06, 2572.61) * mm, v(774.52, 2557.6) * mm, v(798.03, 2542.13) * mm, v(821.42, 2525.97) * mm, v(845, 2509.53) * mm, v(868.36, 2492.27) * mm, v(891.9, 2474.7) * mm, v(915.36, 2456.49) * mm, v(938.8, 2437.68) * mm, v(962.3, 2418.38) * mm, v(985.76, 2398.47) * mm, v(1009.21, 2378) * mm, v(1032.7, 2356.94) * mm, v(1056.12, 2335.26) * mm, v(1079.65, 2313.09) * mm, v(1103.09, 2290.22) * mm, v(1126.51, 2266.74) * mm, v(1150.09, 2242.78) * mm, v(1173.44, 2218) * mm, v(1196.98, 2192.73) * mm, v(1220.45, 2166.76) * mm, v(1243.87, 2140.09) * mm, v(1267.38, 2112.82) * mm, v(1290.85, 2084.85) * mm, v(1314.26, 2056.17) * mm, v(1337.8, 2026.9) * mm, v(1361.24, 1996.83) * mm, v(1384.7, 1966.05) * mm, v(1408.17, 1934.6) * mm, v(1431.66, 1902.38) * mm, v(1455.2, 1869.5) * mm, v(1478.58, 1835.73) * mm, v(1502.05, 1801.27) * mm, v(1525.63, 1766.08) * mm, v(1548.93, 1729.93) * mm, v(1572.51, 1693.13) * mm, v(1595.99, 1655.47) * mm, v(1619.36, 1616.9) * mm, v(1642.9, 1577.62) * mm, v(1666.38, 1537.46) * mm, v(1689.8, 1496.37) * mm, v(1713.26, 1454.42) * mm, v(1736.8, 1411.63) * mm, v(1760.2, 1367.85) * mm, v(1783.68, 1323.2) * mm, v(1807.22, 1277.6) * mm, v(1830.58, 1230.94) * mm, v(1854.07, 1183.38) * mm, v(1877.65, 1134.87) * mm, v(1900.94, 1085.25) * mm, v(1924.53, 1034.72) * mm, v(1948.01, 983.11) * mm, v(1971.37, 930.37) * mm, v(1994.9, 876.63) * mm, v(2018.42, 821.79) * mm, v(2041.78, 765.76) * mm, v(2065.3, 708.67) * mm, v(2088.82, 650.42) * mm, v(2112.18, 590.94) * mm, v(2135.7, 530.32) * mm, v(2159.23, 468.49) * mm, v(2182.58, 405.35) * mm, v(2206.1, 341.03) * mm, v(2229.63, 275.42) * mm, v(2252.98, 208.44) * mm, v(2276.5, 140.2) * mm, v(2300.04, 70.61) * mm, v(2315.44, 23.67) * mm, v(2323.2, 0) * mm]});
            skLineSegment(sketch, "E15.0.1", {"start": v(2323.2, 0) * mm, "end": v(4323.2, 0) * mm});
            skFitSpline(sketch, "E15.0.2", {"points": [v(4323.2, 0) * mm, v(3400, 2700) * mm, v(0, 5904) * mm, v(-3400, 2700) * mm, v(-4323.2, 0) * mm]});
            skLineSegment(sketch, "E15.0.3", {"start": v(-4323.2, 0) * mm, "end": v(-2323.2, 0) * mm});
            skSolve(sketch);
        }
        {
            var Q0;
            Q0 = qSketchRegion(id + "F6", true);
            var Q1;
            Q1=makeQuery(id+"F1.opRevolve","SWEPT_FACE",FACE,{"disambiguationData":[OSD([sQuery(id+"F0.wireOp",EDGE,"E1")])]});
            extrude(context, id + "F7", {"entities" : qUnion([Q0]), "operationType" : NewBodyOperationType.REMOVE, "endBound" : BoundingType.UP_TO_SURFACE, "oppositeDirection" : true, "depth" : 25 * mm, "endBoundEntityFace" : qUnion([Q1]), "offsetDistance" : 25 * mm});
        }
        {
            var Q0;
            Q0=makeQuery(id+"F5.opExtrude","CAP_FACE",FACE,{"disambiguationData":[OSD([sQuery(id+"F4.wireOp",EDGE,"E10"),sQuery(id+"F4.wireOp",EDGE,"E11"),sQuery(id+"F4.wireOp",EDGE,"E13"),sQuery(id+"F4.wireOp",EDGE,"E14.0")])],"isStart":false});
            var sketch = newSketch(context, id + "F8", { "sketchPlane" : qUnion([Q0])});
            skFitSpline(sketch, "E16.0", {"points": [v(-4323.2, 0) * mm, v(-3400, 2700) * mm, v(0, 5904) * mm, v(3400, 2700) * mm, v(4323.2, 0) * mm]});
            skLineSegment(sketch, "E17", {"start": v(-4323.2, 0) * mm, "end": v(4323.2, 0) * mm});
            skSolve(sketch);
        }
        {
            var Q0;
            Q0 = qSketchRegion(id + "F8", true);
            extrude(context, id + "F9", {"entities" : qUnion([Q0]), "operationType" : NewBodyOperationType.ADD, "oppositeDirection" : true, "depth" : 2000 * mm, "offsetDistance" : 25 * mm});
        }
        {
            var Q0;
            Q0=qCreatedBy(makeId("Top.planeOp"),FACE);
            var sketch = newSketch(context, id + "F10", { "sketchPlane" : qUnion([Q0])});
            skLineSegment(sketch, "E18.bottom", {"start": v(100000, -100000) * mm, "end": v(-100000, -100000) * mm});
            skLineSegment(sketch, "E18.top", {"start": v(100000, 100000) * mm, "end": v(-100000, 100000) * mm});
            skLineSegment(sketch, "E18.left", {"start": v(100000, -100000) * mm, "end": v(100000, 100000) * mm});
            skLineSegment(sketch, "E18.right", {"start": v(-100000, -100000) * mm, "end": v(-100000, 100000) * mm});
            skPoint(sketch, "E18.middle", {"position": v(0, 0) * mm});
            skSolve(sketch);
        }
        {
            var Q0;
            Q0 = qSketchRegion(id + "F10", true);
            extrude(context, id + "F11", {"entities" : qUnion([Q0]), "operationType" : NewBodyOperationType.ADD, "oppositeDirection" : true, "depth" : 200000 * mm, "offsetDistance" : 25 * mm});
        }
    });
